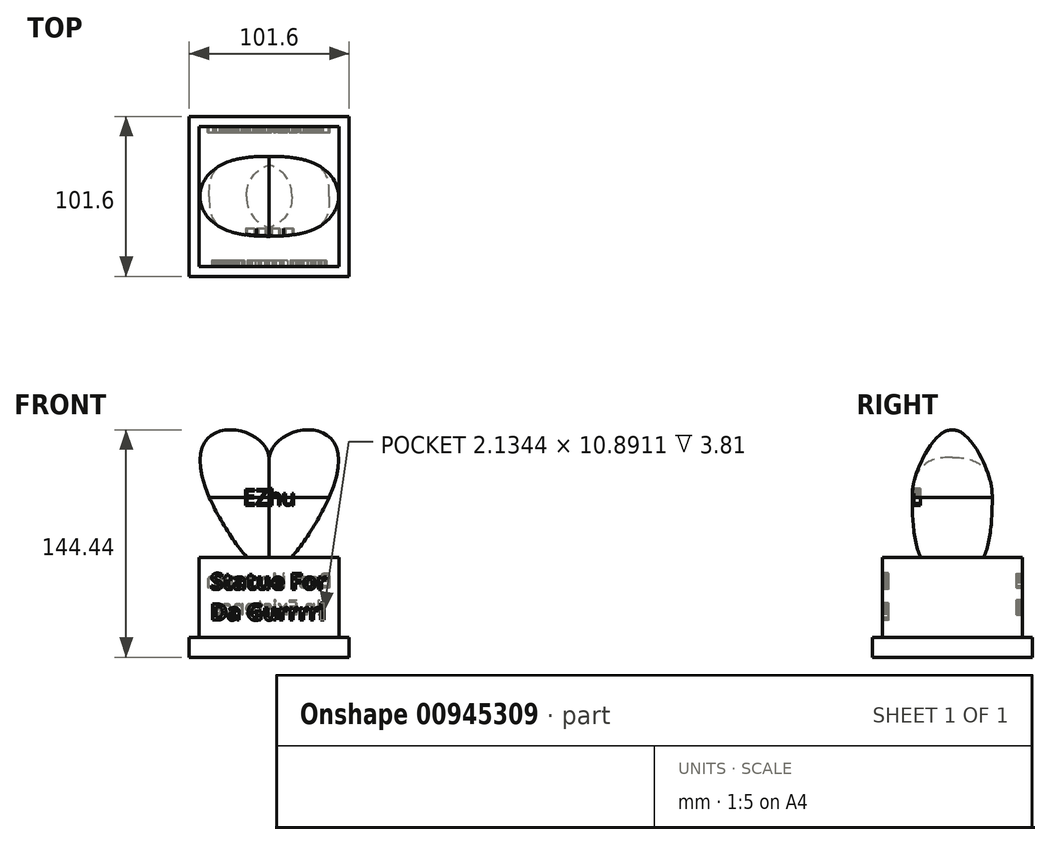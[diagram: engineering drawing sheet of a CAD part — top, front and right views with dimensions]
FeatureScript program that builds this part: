
annotation { "Feature Type Name" : "Feature", "Feature Type Description" : "" }
export const myFeature = defineFeature(function(context is Context, id is Id, definition is map)
    precondition{}
    {
        {
            var Q0;
            Q0=qCreatedBy(makeId("Top.planeOp"),FACE);
            var sketch = newSketch(context, id + "F0", { "sketchPlane" : qUnion([Q0])});
            skLineSegment(sketch, "E0.bottom", {"start": v(0, 0) * mm, "end": v(-50.8, 0) * mm});
            skLineSegment(sketch, "E0.top", {"start": v(0, -50.8) * mm, "end": v(-50.8, -50.8) * mm});
            skLineSegment(sketch, "E0.left", {"start": v(0, 0) * mm, "end": v(0, -50.8) * mm});
            skLineSegment(sketch, "E0.right", {"start": v(-50.8, 0) * mm, "end": v(-50.8, -50.8) * mm});
            skSolve(sketch);
        }
        {
            var Q0;
            Q0 = qSketchRegion(id + "F0", true);
            extrude(context, id + "F1", {"entities" : qUnion([Q0]), "depth" : 12.7 * mm, "offsetDistance" : 25.4 * mm});
        }
        {
            var Q0;
            Q0=makeQuery(id+"F1.opExtrude","CAP_FACE",FACE,{"disambiguationData":[OSD([sQuery(id+"F0.wireOp",EDGE,"E0.bottom"),sQuery(id+"F0.wireOp",EDGE,"E0.top"),sQuery(id+"F0.wireOp",EDGE,"E0.left"),sQuery(id+"F0.wireOp",EDGE,"E0.right")])],"isStart":false});
            var sketch = newSketch(context, id + "F2", { "sketchPlane" : qUnion([Q0])});
            skLineSegment(sketch, "E1.bottom", {"start": v(0, 0) * mm, "end": v(-44.45, 0) * mm});
            skLineSegment(sketch, "E1.top", {"start": v(0, -44.45) * mm, "end": v(-44.45, -44.45) * mm});
            skLineSegment(sketch, "E1.left", {"start": v(0, 0) * mm, "end": v(0, -44.45) * mm});
            skLineSegment(sketch, "E1.right", {"start": v(-44.45, 0) * mm, "end": v(-44.45, -44.45) * mm});
            skSolve(sketch);
        }
        {
            var Q0;
            Q0 = qSketchRegion(id + "F2", true);
            extrude(context, id + "F3", {"entities" : qUnion([Q0]), "operationType" : NewBodyOperationType.ADD, "depth" : 50.8 * mm, "offsetDistance" : 25.4 * mm});
        }
        {
            var Q0;
            Q0=qCreatedBy(makeId("Right.planeOp"),FACE);
            var sketch = newSketch(context, id + "F4", { "sketchPlane" : qUnion([Q0])});
            skPoint(sketch, "E2.0", {"position": v(0, 63.5) * mm});
            skLineSegment(sketch, "E3", {"start": v(0, 63.5) * mm, "end": v(0, 50.8) * mm, "construction": true});
            skLineSegment(sketch, "E4", {"start": v(0, 50.8) * mm, "end": v(0, 101.6) * mm});
            skLineSegment(sketch, "E5", {"start": v(0, 101.6) * mm, "end": v(-25.4, 101.6) * mm});
            skFitSpline(sketch, "E6", {"points": [v(-25.4, 101.6) * mm, v(0, 50.8) * mm], "startDerivative": vector(0, -89.45) * mm, "endDerivative": vector(63.97, 0) * mm});
            skSolve(sketch);
        }
        {
            var Q0;
            Q0=qCreatedBy(makeId("Right.planeOp"),FACE);
            var sketch = newSketch(context, id + "F5", { "sketchPlane" : qUnion([Q0])});
            skLineSegment(sketch, "E7.0", {"start": v(0, 101.6) * mm, "end": v(-25.4, 101.6) * mm});
            skLineSegment(sketch, "E8", {"start": v(0, 101.6) * mm, "end": v(0, 127) * mm});
            skFitSpline(sketch, "E9", {"points": [v(0, 127) * mm, v(-25.4, 101.6) * mm], "startDerivative": vector(-46.3, 0) * mm, "endDerivative": vector(0, -58.74) * mm});
            skSolve(sketch);
        }
        {
            var Q0;
            Q0=qCreatedBy(makeId("Top.planeOp"),FACE);
            var Q1;
            Q1=sQuery(id+"F4.wireOp",VERTEX,"E4.end");
            cPlane(context, id + "F6", {"entities" : qUnion([Q0, Q1]), "cplaneType" : CPlaneType.PLANE_POINT, "offset" : 25.4 * mm, "width" : 152.4 * mm, "height" : 152.4 * mm});
        }
        {
            var Q0;
            Q0=qCreatedBy(id+"F6.planeOp",FACE);
            var sketch = newSketch(context, id + "F7", { "sketchPlane" : qUnion([Q0])});
            skLineSegment(sketch, "E10.0", {"start": v(0, 0) * mm, "end": v(0, -25.4) * mm});
            skLineSegment(sketch, "E11", {"start": v(0, 0) * mm, "end": v(-38.1, 0) * mm});
            skFitSpline(sketch, "E12", {"points": [v(-38.1, 0) * mm, v(0, -25.4) * mm], "startDerivative": vector(0, -37.4) * mm, "endDerivative": vector(114.3, 0) * mm});
            skSolve(sketch);
        }
        {
            var Q0;
            Q0=qCreatedBy(makeId("Front.planeOp"),FACE);
            var sketch = newSketch(context, id + "F8", { "sketchPlane" : qUnion([Q0])});
            skPoint(sketch, "E13.0", {"position": v(-38.1, 101.6) * mm});
            skPoint(sketch, "E14.0", {"position": v(0, 127) * mm});
            skPoint(sketch, "E15.0", {"position": v(0, 50.8) * mm});
            skFitSpline(sketch, "E16", {"points": [v(-38.1, 101.6) * mm, v(0, 127) * mm], "startDerivative": vector(-73.72, 165.9) * mm, "endDerivative": vector(10.78, -71.56) * mm});
            skFitSpline(sketch, "E17", {"points": [v(-38.1, 101.6) * mm, v(0, 50.8) * mm], "startDerivative": vector(33.5, -75.4) * mm, "endDerivative": vector(17.44, 0) * mm});
            skLineSegment(sketch, "E18", {"start": v(-62.67, 156.9) * mm, "end": v(-38.1, 101.6) * mm, "construction": true});
            skLineSegment(sketch, "E19", {"start": v(-38.1, 101.6) * mm, "end": v(-29.83, 83) * mm, "construction": true});
            skSolve(sketch);
        }
        {
            var Q0;
            Q0=makeQuery(id+"F5.imprint","IMPRINT",FACE,{"disambiguationData":[TD([[makeQuery(id+"F5.imprint","IMPRINT",EDGE,{"derivedFrom":sQuery(id+"F5.wireOp",EDGE,"E7.0")}),-1.0]])]});
            var Q1;
            Q1=makeQuery(id+"F7.imprint","IMPRINT",FACE,{"disambiguationData":[TD([[makeQuery(id+"F7.imprint","IMPRINT",EDGE,{"derivedFrom":sQuery(id+"F7.wireOp",EDGE,"E10.0")}),-1.0]])]});
            var Q2;
            Q2=sQuery(id+"F8.wireOp",EDGE,"E16");
            loft(context, id + "F9", {"addGuides" : true, "sheetProfilesArray" : [{ "sheetProfileEntities" : qUnion([Q0]) }, { "sheetProfileEntities" : qUnion([Q1]) }], "guidesArray" : [{ "guideEntities" : qUnion([Q2]), "guideDerivativeType" : LoftGuideDerivativeType.DEFAULT, "guideDerivativeMagnitude" : 1 }]});
        }
        {
            var Q0;
            Q0=makeQuery(id+"F4.imprint","IMPRINT",FACE,{"disambiguationData":[TD([[makeQuery(id+"F4.imprint","IMPRINT",EDGE,{"derivedFrom":sQuery(id+"F4.wireOp",EDGE,"E4")}),1.0]])]});
            var Q1;
            Q1=makeQuery(id+"F7.imprint","IMPRINT",FACE,{"disambiguationData":[TD([[makeQuery(id+"F7.imprint","IMPRINT",EDGE,{"derivedFrom":sQuery(id+"F7.wireOp",EDGE,"E10.0")}),-1.0]])]});
            var Q2;
            Q2=sQuery(id+"F8.wireOp",EDGE,"E17");
            loft(context, id + "F10", {"addGuides" : true, "sheetProfilesArray" : [{ "sheetProfileEntities" : qUnion([Q0]) }, { "sheetProfileEntities" : qUnion([Q1]) }], "guidesArray" : [{ "guideEntities" : qUnion([Q2]), "guideDerivativeType" : LoftGuideDerivativeType.DEFAULT, "guideDerivativeMagnitude" : 1 }]});
        }
        {
            var Q0;
            Q0=makeQuery(id+"F1.opExtrude","SWEPT_BODY",BODY,{"disambiguationData":[OSD([sQuery(id+"F0.wireOp",EDGE,"E0.bottom"),sQuery(id+"F0.wireOp",EDGE,"E0.top"),sQuery(id+"F0.wireOp",EDGE,"E0.left"),sQuery(id+"F0.wireOp",EDGE,"E0.right")])]});
            var Q1;
            Q1=makeQuery(id+"F10.opLoft","SWEPT_BODY",BODY,{"disambiguationData":[OSD([makeQuery(id+"F4.imprint","IMPRINT",FACE,{"disambiguationData":[TD([[makeQuery(id+"F4.imprint","IMPRINT",EDGE,{"derivedFrom":sQuery(id+"F4.wireOp",EDGE,"E4")}),1.0]])]}),makeQuery(id+"F7.imprint","IMPRINT",FACE,{"disambiguationData":[TD([[makeQuery(id+"F7.imprint","IMPRINT",EDGE,{"derivedFrom":sQuery(id+"F7.wireOp",EDGE,"E10.0")}),-1.0]])]}),sQuery(id+"F8.wireOp",EDGE,"E17")])]});
            var Q2;
            Q2=makeQuery(id+"F9.opLoft","SWEPT_BODY",BODY,{"disambiguationData":[OSD([makeQuery(id+"F5.imprint","IMPRINT",FACE,{"disambiguationData":[TD([[makeQuery(id+"F5.imprint","IMPRINT",EDGE,{"derivedFrom":sQuery(id+"F5.wireOp",EDGE,"E7.0")}),-1.0]])]}),makeQuery(id+"F7.imprint","IMPRINT",FACE,{"disambiguationData":[TD([[makeQuery(id+"F7.imprint","IMPRINT",EDGE,{"derivedFrom":sQuery(id+"F7.wireOp",EDGE,"E10.0")}),-1.0]])]}),sQuery(id+"F8.wireOp",EDGE,"E16")])]});
            booleanBodies(context, id + "F11", {"operationType" : BooleanOperationType.UNION, "tools" : qUnion([Q0, Q1, Q2])});
        }
        {
            var Q0;
            Q0=makeQuery(id+"F1.opExtrude","SWEPT_BODY",BODY,{"disambiguationData":[OSD([sQuery(id+"F0.wireOp",EDGE,"E0.bottom"),sQuery(id+"F0.wireOp",EDGE,"E0.top"),sQuery(id+"F0.wireOp",EDGE,"E0.left"),sQuery(id+"F0.wireOp",EDGE,"E0.right")])]});
            var Q1;
            Q1=makeQuery(id+"F11.opBoolean","MERGE",FACE,{"derivedFrom":[makeQuery(id+"F3.boolean.opBoolean","MERGE",FACE,{"derivedFrom":[makeQuery(id+"F1.opExtrude","SWEPT_FACE",FACE,{"disambiguationData":[OSD([sQuery(id+"F0.wireOp",EDGE,"E0.left")])]}),makeQuery(id+"F3.opExtrude","SWEPT_FACE",FACE,{"disambiguationData":[OSD([sQuery(id+"F2.wireOp",EDGE,"E1.left")])]})]}),makeQuery(id+"F9.opLoft","CAP_FACE",FACE,{"disambiguationData":[OSD([makeQuery(id+"F5.imprint","IMPRINT",FACE,{"disambiguationData":[TD([[makeQuery(id+"F5.imprint","IMPRINT",EDGE,{"derivedFrom":sQuery(id+"F5.wireOp",EDGE,"E7.0")}),-1.0]])]})])],"isStart":true}),makeQuery(id+"F10.opLoft","CAP_FACE",FACE,{"disambiguationData":[OSD([makeQuery(id+"F4.imprint","IMPRINT",FACE,{"disambiguationData":[TD([[makeQuery(id+"F4.imprint","IMPRINT",EDGE,{"derivedFrom":sQuery(id+"F4.wireOp",EDGE,"E4")}),1.0]])]})])],"isStart":true})]});
            mirror(context, id + "F12", {"operationType" : NewBodyOperationType.ADD, "entities" : qUnion([Q0]), "mirrorPlane" : qUnion([Q1])});
        }
        {
            var Q0;
            Q0=makeQuery(id+"F1.opExtrude","SWEPT_BODY",BODY,{"disambiguationData":[OSD([sQuery(id+"F0.wireOp",EDGE,"E0.bottom"),sQuery(id+"F0.wireOp",EDGE,"E0.top"),sQuery(id+"F0.wireOp",EDGE,"E0.left"),sQuery(id+"F0.wireOp",EDGE,"E0.right")])]});
            var Q1;
            {var subQ0=sQuery(id+"F7.wireOp",EDGE,"E12");var subQ1=sQuery(id+"F7.wireOp",EDGE,"E11");var subQ2=sQuery(id+"F7.wireOp",EDGE,"E10.0");var subQ3=makeQuery(id+"F11.opBoolean","MERGE",FACE,{"derivedFrom":[makeQuery(id+"F3.boolean.opBoolean","MERGE",FACE,{"derivedFrom":[makeQuery(id+"F1.opExtrude","SWEPT_FACE",FACE,{"disambiguationData":[OSD([sQuery(id+"F0.wireOp",EDGE,"E0.bottom")])]}),makeQuery(id+"F3.opExtrude","SWEPT_FACE",FACE,{"disambiguationData":[OSD([sQuery(id+"F2.wireOp",EDGE,"E1.bottom")])]})]}),makeQuery(id+"F9.opLoft","SWEPT_FACE",FACE,{"disambiguationData":[OSD([sQuery(id+"F5.wireOp",EDGE,"E7.0"),sQuery(id+"F5.wireOp",EDGE,"E8"),sQuery(id+"F5.wireOp",EDGE,"E9"),subQ2,subQ1,subQ0,sQuery(id+"F8.wireOp",EDGE,"E16")])]}),makeQuery(id+"F10.opLoft","SWEPT_FACE",FACE,{"disambiguationData":[OSD([sQuery(id+"F4.wireOp",EDGE,"E4"),sQuery(id+"F4.wireOp",EDGE,"E5"),sQuery(id+"F4.wireOp",EDGE,"E6"),subQ2,subQ1,subQ0,sQuery(id+"F8.wireOp",EDGE,"E17")])]})]});Q1=makeQuery(id+"F12.boolean.opBoolean","MERGE",FACE,{"derivedFrom":[subQ3,makeQuery(id+"F12.opPattern","COPY",FACE,{"derivedFrom":subQ3,"instanceName":"1"})]});}
            mirror(context, id + "F13", {"operationType" : NewBodyOperationType.ADD, "entities" : qUnion([Q0]), "mirrorPlane" : qUnion([Q1])});
        }
        {
            var Q0;
            {var subQ0=makeQuery(id+"F3.opExtrude","SWEPT_FACE",FACE,{"disambiguationData":[OSD([sQuery(id+"F2.wireOp",EDGE,"E1.top")])]});Q0=makeQuery(id+"F12.boolean.opBoolean","MERGE",FACE,{"derivedFrom":[subQ0,makeQuery(id+"F12.opPattern","COPY",FACE,{"derivedFrom":subQ0,"instanceName":"1"})]});}
            var sketch = newSketch(context, id + "F14", { "sketchPlane" : qUnion([Q0])});
            skText(sketch, "E20", { "text": "Statue For \nDa Gurrrrl", "fontName": "OpenSans-Bold.ttf"});
            skFitSpline(sketch, "E21.0.3", {"points": [v(0, 63.5) * mm, v(4.81, 63.5) * mm, v(9.62, 63.5) * mm, v(14.43, 63.5) * mm]});
            skLineSegment(sketch, "E22", {"start": v(0, 63.5) * mm, "end": v(0, 53.34) * mm, "construction": true});
            const initialGuessF14  = {"E20": [-0.03726, 0.04302, 1, 0, 0.01032]};
            skSetInitialGuess(sketch, initialGuessF14);
            skSolve(sketch);
        }
        {
            var Q0;
            Q0 = qSketchRegion(id + "F14", true);
            extrude(context, id + "F15", {"entities" : qUnion([Q0]), "operationType" : NewBodyOperationType.REMOVE, "oppositeDirection" : true, "depth" : 3.8 * mm, "offsetDistance" : 25.4 * mm});
        }
        {
            var Q0;
            {var subQ0=makeQuery(id+"F3.opExtrude","SWEPT_FACE",FACE,{"disambiguationData":[OSD([sQuery(id+"F2.wireOp",EDGE,"E1.top")])]});Q0=makeQuery(id+"F13.opPattern","COPY",FACE,{"derivedFrom":makeQuery(id+"F12.boolean.opBoolean","MERGE",FACE,{"derivedFrom":[subQ0,makeQuery(id+"F12.opPattern","COPY",FACE,{"derivedFrom":subQ0,"instanceName":"1"})]}),"instanceName":"1"});}
            var sketch = newSketch(context, id + "F16", { "sketchPlane" : qUnion([Q0])});
            skFitSpline(sketch, "E23.0.3", {"points": [v(0, 63.5) * mm, v(4.81, 63.5) * mm, v(9.62, 63.5) * mm, v(14.43, 63.5) * mm]});
            skText(sketch, "E24", { "text": "Best Hooman \n  In Existence", "fontName": "OpenSans-Regular.ttf"});
            skLineSegment(sketch, "E25", {"start": v(0, 63.5) * mm, "end": v(0, 53.34) * mm, "construction": true});
            const initialGuessF16  = {"E24": [-0.04, 0.04424, 1, 0, 0.0091]};
            skSetInitialGuess(sketch, initialGuessF16);
            skSolve(sketch);
        }
        {
            var Q0;
            Q0 = qSketchRegion(id + "F16", true);
            extrude(context, id + "F17", {"entities" : qUnion([Q0]), "operationType" : NewBodyOperationType.REMOVE, "oppositeDirection" : true, "depth" : 3.8 * mm, "offsetDistance" : 25.4 * mm});
        }
        {
            var Q0;
            Q0=qCreatedBy(makeId("Front.planeOp"),FACE);
            var Q1;
            Q1=sQuery(id+"F4.wireOp",VERTEX,"E5.end");
            cPlane(context, id + "F18", {"entities" : qUnion([Q0, Q1]), "cplaneType" : CPlaneType.PLANE_POINT, "offset" : 25.4 * mm, "width" : 152.4 * mm, "height" : 152.4 * mm});
        }
        {
            var Q0;
            Q0=qCreatedBy(id+"F18.planeOp",FACE);
            var sketch = newSketch(context, id + "F19", { "sketchPlane" : qUnion([Q0])});
            skText(sketch, "E26", { "text": "EZhu", "fontName": "OpenSans-Regular.ttf"});
            skPoint(sketch, "E27.0", {"position": v(0, 101.6) * mm});
            skLineSegment(sketch, "E28", {"start": v(0, 101.6) * mm, "end": v(0, 106.68) * mm, "construction": true});
            const initialGuessF19  = {"E26": [-0.01646, 0.09652, 1, 0, 0.01016]};
            skSetInitialGuess(sketch, initialGuessF19);
            skSolve(sketch);
        }
        {
            var Q0;
            Q0 = qSketchRegion(id + "F19", true);
            extrude(context, id + "F20", {"entities" : qUnion([Q0]), "operationType" : NewBodyOperationType.REMOVE, "oppositeDirection" : true, "depth" : 5.08 * mm, "offsetDistance" : 25.4 * mm});
        }
    });
